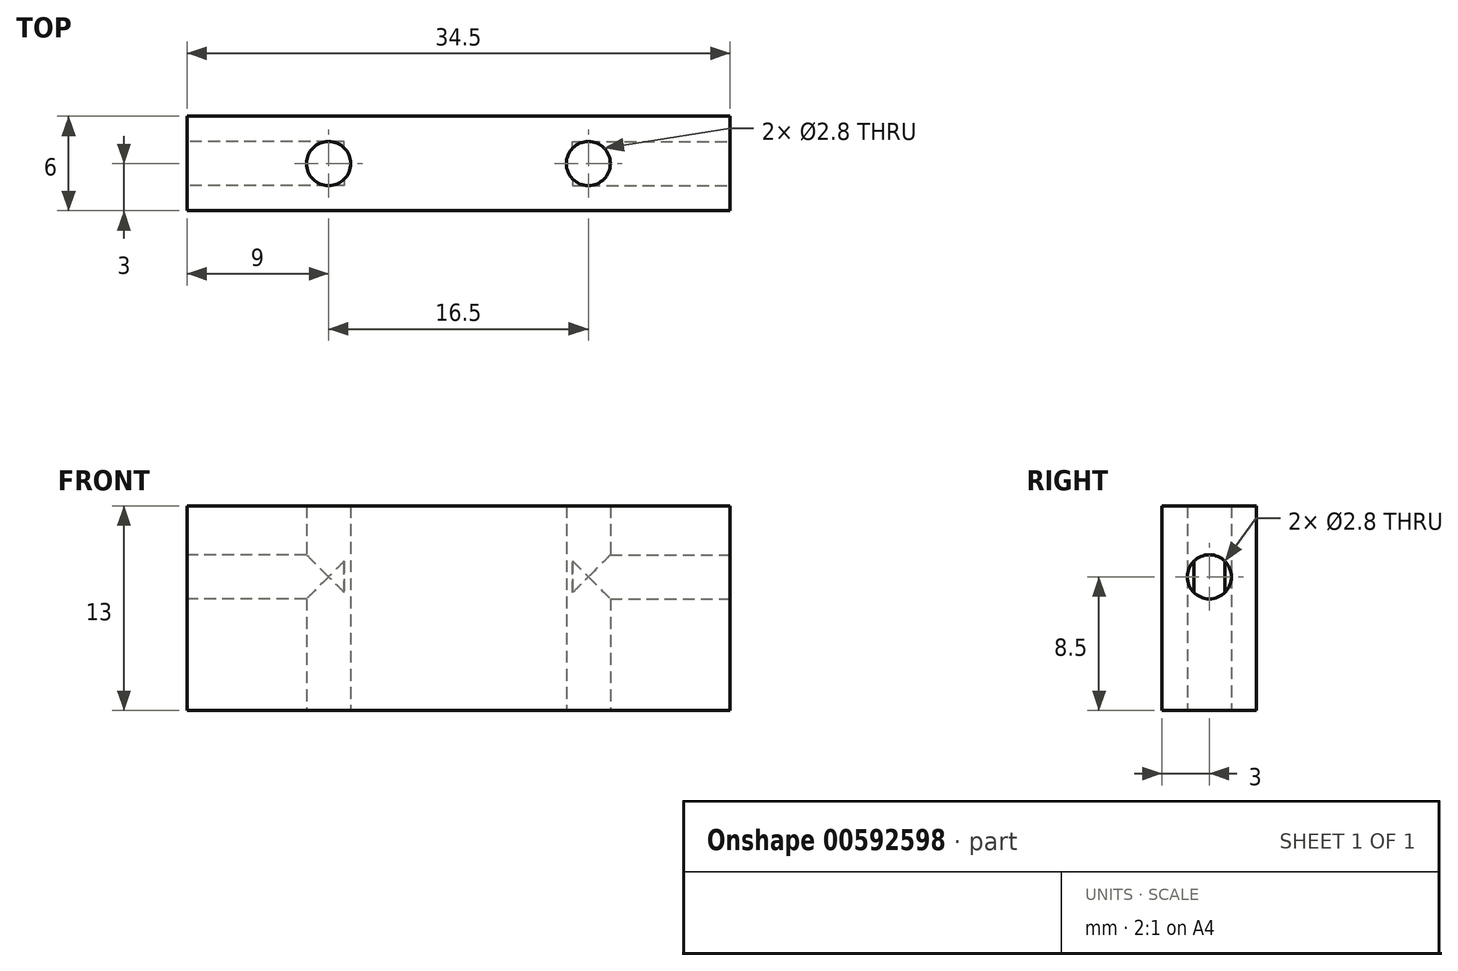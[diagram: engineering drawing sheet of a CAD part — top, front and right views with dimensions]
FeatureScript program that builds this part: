
annotation { "Feature Type Name" : "Feature", "Feature Type Description" : "" }
export const myFeature = defineFeature(function(context is Context, id is Id, definition is map)
    precondition{}
    {
        {
            var Q0;
            Q0=qCreatedBy(makeId("Top.planeOp"),FACE);
            var sketch = newSketch(context, id + "F0", { "sketchPlane" : qUnion([Q0])});
            skLineSegment(sketch, "E0.bottom", {"start": v(0, 0) * mm, "end": v(34.5, 0) * mm});
            skLineSegment(sketch, "E0.top", {"start": v(0, 6) * mm, "end": v(34.5, 6) * mm});
            skLineSegment(sketch, "E0.left", {"start": v(0, 0) * mm, "end": v(0, 6) * mm});
            skLineSegment(sketch, "E0.right", {"start": v(34.5, 0) * mm, "end": v(34.5, 6) * mm});
            skCircle(sketch, "E1", {"center": v(9, 3) * mm, "radius": 1.4 * mm});
            skPoint(sketch, "E1.centerSnap0", {"position": v(0, 3) * mm});
            skCircle(sketch, "E2", {"center": v(25.5, 3) * mm, "radius": 1.4 * mm});
            skSolve(sketch);
        }
        {
            var Q0;
            Q0=makeQuery(id+"F0.imprint","IMPRINT",FACE,{"disambiguationData":[TD([[makeQuery(id+"F0.imprint","IMPRINT",EDGE,{"derivedFrom":sQuery(id+"F0.wireOp",EDGE,"E0.bottom")}),1.0]])]});
            extrude(context, id + "F1", {"entities" : qUnion([Q0]), "depth" : 13 * mm, "offsetDistance" : 25 * mm});
        }
        {
            var Q0;
            Q0=makeQuery(id+"F1.opExtrude","SWEPT_FACE",FACE,{"disambiguationData":[OSD([sQuery(id+"F0.wireOp",EDGE,"E0.left")])]});
            var sketch = newSketch(context, id + "F2", { "sketchPlane" : qUnion([Q0])});
            skLineSegment(sketch, "E3.0.0", {"start": v(-6, 0) * mm, "end": v(0, 0) * mm});
            skLineSegment(sketch, "E3.0.1", {"start": v(0, 0) * mm, "end": v(0, 13) * mm});
            skLineSegment(sketch, "E3.0.2", {"start": v(0, 13) * mm, "end": v(-6, 13) * mm});
            skLineSegment(sketch, "E3.0.3", {"start": v(-6, 13) * mm, "end": v(-6, 0) * mm});
            skCircle(sketch, "E4", {"center": v(-3, 8.5) * mm, "radius": 1.4 * mm});
            skPoint(sketch, "E4.centerSnap0", {"position": v(-3, 13) * mm});
            skSolve(sketch);
        }
        {
            var Q0;
            Q0=makeQuery(id+"F2.imprint","IMPRINT",FACE,{"disambiguationData":[TD([[makeQuery(id+"F2.imprint","IMPRINT",EDGE,{"derivedFrom":sQuery(id+"F2.wireOp",EDGE,"E4")}),1.0]])]});
            extrude(context, id + "F3", {"entities" : qUnion([Q0]), "operationType" : NewBodyOperationType.REMOVE, "oppositeDirection" : true, "depth" : 10 * mm, "offsetDistance" : 25 * mm});
        }
        {
            var Q0;
            Q0=makeQuery(id+"F1.opExtrude","SWEPT_FACE",FACE,{"disambiguationData":[OSD([sQuery(id+"F0.wireOp",EDGE,"E0.right")])]});
            var sketch = newSketch(context, id + "F4", { "sketchPlane" : qUnion([Q0])});
            skCircle(sketch, "E5", {"center": v(3, 8.5) * mm, "radius": 1.4 * mm});
            skPoint(sketch, "E5.centerSnap0", {"position": v(3, 0) * mm});
            skSolve(sketch);
        }
        {
            var Q0;
            Q0=makeQuery(id+"F4.imprint","IMPRINT",FACE,{"disambiguationData":[TD([[makeQuery(id+"F4.imprint","IMPRINT",EDGE,{"derivedFrom":sQuery(id+"F4.wireOp",EDGE,"E5")}),1.0]])]});
            extrude(context, id + "F5", {"entities" : qUnion([Q0]), "operationType" : NewBodyOperationType.REMOVE, "oppositeDirection" : true, "depth" : 10 * mm, "offsetDistance" : 25 * mm});
        }
    });
